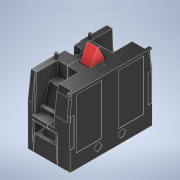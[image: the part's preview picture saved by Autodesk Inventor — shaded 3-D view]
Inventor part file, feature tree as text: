
AUTODESK INVENTOR PART (.ipt)
format: ipt  version: 2022 (Build 260153000, 153)  size: 3,170,816 bytes
history: native  units: mm
features: extrude x34, sketch x30, projected_geometry x12, chamfer x5, plane x3, emboss x1
ambient origin geometry x8: Origin, YZ Plane, XZ Plane, XY Plane, X Axis, Y Axis, Z Axis, Center Point
bodies: Solid1 (feature_tree)
feature tree (85):
  extrude  "Extrusion1"  Depth=2.0mm
  sketch  "Sketch2"  dims[d8=7.0mm d10=6.0mm]
  extrude  "Extrusion2"  Depth=6.0mm
  extrude  "Extrusion3"  Depth=1.0mm
  extrude  "Extrusion5"  Depth=3.0mm
  extrude  "Extrusion9"  Depth=10.5mm
  sketch  "Sketch6"  dims[d15=3.0mm d16=3.0mm]
  sketch  "Sketch8"  dims[d17=10.5mm d18=10.5mm]
  sketch  "Sketch9"  dims[d19=5.0mm d20=0.0mm d21=5.0mm d22=0.0mm]
  extrude  "Extrusion11"  Depth=5.0mm TaperAngle=0.0deg
  extrude  "Extrusion14"  Depth=3.0mm
  sketch  "Sketch12"  dims[d27=2.0mm d29=0.3mm]
  extrude  "Extrusion15"  Depth=2.0mm
  extrude  "Extrusion16"  Depth=4.0mm
  sketch  "Sketch13"  dims[d30=4.0mm d31=4.0mm]
  extrude  "Extrusion17"  Depth=1.0mm
  extrude  "Extrusion18"  TaperAngle=0.0deg  [1 undecoded]
  extrude  "Extrusion19"  Depth=6.0mm
  extrude  "Extrusion20"  Depth=6.5mm
  plane  "Work Plane1"
  sketch  "Sketch16"  dims[d45=2.0mm d46=0.0mm d57=6.0mm]
  extrude  "Extrusion21"  Depth=6.5mm
  extrude  "Extrusion22"  Depth=6.0mm
  extrude  "Extrusion23"  Depth=5.5mm
  plane  "Work Plane2"
  sketch  "Sketch18"  dims[d60=14.2mm d61=6.5mm]
  extrude  "Extrusion24"  Depth=5.0mm
  extrude  "Extrusion25"  Depth=5.5mm
  chamfer  "Chamfer2"  Distance=6.0mm
  chamfer  "Chamfer3"  Distance=0.2mm
  extrude  "Extrusion26"  TaperAngle=45.0deg  [1 undecoded]
  extrude  "Extrusion27"  TaperAngle=45.0deg  [1 undecoded]
  extrude  "Extrusion28"  Depth=3.7mm TaperAngle=0.0deg
  extrude  "Extrusion29"  Depth=3.0mm
  extrude  "Extrusion30"  Depth=0.5mm
  extrude  "Extrusion31"  Depth=2.4mm
  chamfer  "Chamfer4"  [1 undecoded]
  extrude  "Extrusion32"  Depth=4.0mm TaperAngle=0.0deg
  extrude  "Extrusion33"  TaperAngle=0.0deg  [1 undecoded]
  sketch  "Sketch25"  dims[d74=3.35mm]
  extrude  "Extrusion34"  Depth=1.0mm
  extrude  "Extrusion35"  Depth=18.0mm
  extrude  "Extrusion36"  Depth=9.0mm
  sketch  "Sketch27"  dims[d76=4.5mm]
  extrude  "Extrusion37"  Depth=3.0mm
  extrude  "Extrusion38"  Depth=9.0mm
  extrude  "Extrusion39"  Depth=6.0mm
  emboss  "Emboss1"
  plane  "Work Plane4"
  extrude  "Extrusion40"  Depth=2.0mm
  sketch  "Sketch33"  dims[d90=6.0mm]
  chamfer  "Chamfer5"  Distance=10.0mm
  chamfer  "Chamfer6"  Distance=0.1mm
  extrude  "Extrusion41"  Depth=0.09mm TaperAngle=0.0deg
  sketch  "Sketch1"  dims[d5=15.0mm d6=0.0mm d7=2.0mm]
  projected_geometry  "Projected Loop1"
  sketch  "Sketch4"  dims[d11=6.0mm d14=1.0mm]
  sketch  "Sketch11"  dims[d25=3.5mm d26=3.0mm]
  sketch  "Sketch14"  dims[d32=0.5mm d33=0.0mm d42=1.0mm]
  sketch  "Sketch15"  dims[d43=1.0mm d44=0.0mm]
  sketch  "Sketch17"  dims[d58=1.0mm d59=6.5mm]
  projected_geometry  "Projected Loop2"
  projected_geometry  "Projected Loop3"
  projected_geometry  "Projected Loop4"
  sketch  "Sketch19"  dims[d62=1.0mm d64=6.0mm]
  sketch  "Sketch20"  dims[d66=4.5mm d67=5.5mm]
  projected_geometry  "Projected Loop5"
  sketch  "Sketch21"  dims[d68=5.0mm d69=5.0mm]
  sketch  "Sketch22"  dims[d70=4.5mm d71=5.5mm]
  projected_geometry  "Projected Loop6"
  projected_geometry  "Projected Loop7"
  projected_geometry  "Projected Loop8"
  sketch  "Sketch23"  dims[d72=4.5mm]
  sketch  "Sketch24"  dims[d73=0.1mm]
  projected_geometry  "Projected Loop9"
  projected_geometry  "Projected Loop10"
  projected_geometry  "Projected Loop11"
  sketch  "Sketch26"  dims[d75=3.35mm]
  sketch  "Sketch28"  dims[d77=4.0mm]
  sketch  "Sketch29"  dims[d78=6.5mm]
  sketch  "Sketch30"  dims[d79=4.0mm d80=6.0mm d81=0.0mm]
  sketch  "Sketch31"  dims[d88=3.5mm]
  sketch  "Sketch32"  dims[d89=3.5mm]
  sketch  "Sketch34"  dims[d92=3.0mm d93=0.2mm d94=45.0deg d95=45.0deg d96=3.7mm d97=0.0mm d99=3.0mm d100=0.5mm d101=2.4mm d102=0.0mm d103=4.0mm d104=0.0mm d105=0.0mm d106=0.0mm d110=1.0mm d111=18.0mm d112=9.0mm d113=3.0mm d114=9.0mm d115=6.0mm d116=2.0mm d117=10.0mm d118=0.1mm d119=0.0mm d120=0.09mm d121=0.0mm d122=2.5mm d123=2.5mm d125=2.0mm d126=2.0mm d127=0.09mm d128=0.0mm d130=0.0mm d131=1.173362mm d132=0.5mm d133=1.0mm d134=0.0mm d135=-13.0mm d136=5.5mm d137=3.0mm d138=8.0mm d139=3.0mm d140=18.850282mm d141=2.0mm d142=10.0mm d143=5.0mm d144=0.0mm d145=5.0mm d146=0.0mm d147=10.0mm d148=0.0mm d149=-3.5mm d150=2.0mm d151=3.5mm d152=10.0mm d153=0.0mm d154=0.7mm d155=10.0mm d156=0.0mm d157=0.9mm d158=0.5mm d159=45.0deg d160=0.5mm d161=0.5mm d162=45.0deg d163=0.08mm d164=0.0mm d166=0.08mm d167=0.08mm d168=10.0mm d169=0.0mm d170=5.0mm d171=0.0mm d172=5.0mm d173=0.0mm d174=56.0mm d175=0.0mm d176=10.0mm d177=0.0mm d178=0.8mm d179=10.0mm d180=0.0mm d181=0.5mm d182=0.5mm d183=45.0deg d184=0.5mm d185=0.0mm d186=0.1mm d187=0.1mm d189=90.0deg d190=3.0mm d191=0.1mm d192=0.1mm d194=0.1mm d196=4.4mm d197=1.25mm d198=6.0mm d199=0.1mm d200=3.75mm d201=14.0mm d202=4.4mm d203=0.35mm d204=0.5mm d205=0.0mm d206=2.0mm d207=3.0mm d208=0.5mm d209=0.0mm d210=0.5mm d211=0.0mm d212=2.0mm d213=2.0mm d214=0.0mm d215=0.0mm d216=0.5mm d217=0.0mm d218=5.0mm d219=0.0mm d220=5.0mm d221=0.0mm d222=1.0mm d223=1.5mm d224=0.5mm d225=0.0mm d227=0.1mm d228=0.2mm d229=0.0mm d231=-1.0mm d233=5.0mm d234=5.0mm d237=0.0mm d238=6.5mm d239=0.75mm d240=3.6mm d241=0.0mm d242=2.0mm d243=0.5mm d244=45.0deg d245=2.0mm d246=0.5mm d247=45.0deg d249=3.6mm d250=0.0mm d251=6.0mm d252=6.0mm d253=14.6mm d254=14.6mm d38=0.5mm d39=0.872665mm d40=0.5mm d41=0.872665mm]
  projected_geometry  "Projected Loop12"
note: 5 required parameter values undecoded (feature->parameter linkage not recoverable at this tier; creation-order binding heuristic only, values carry confidence <= 0.55)
